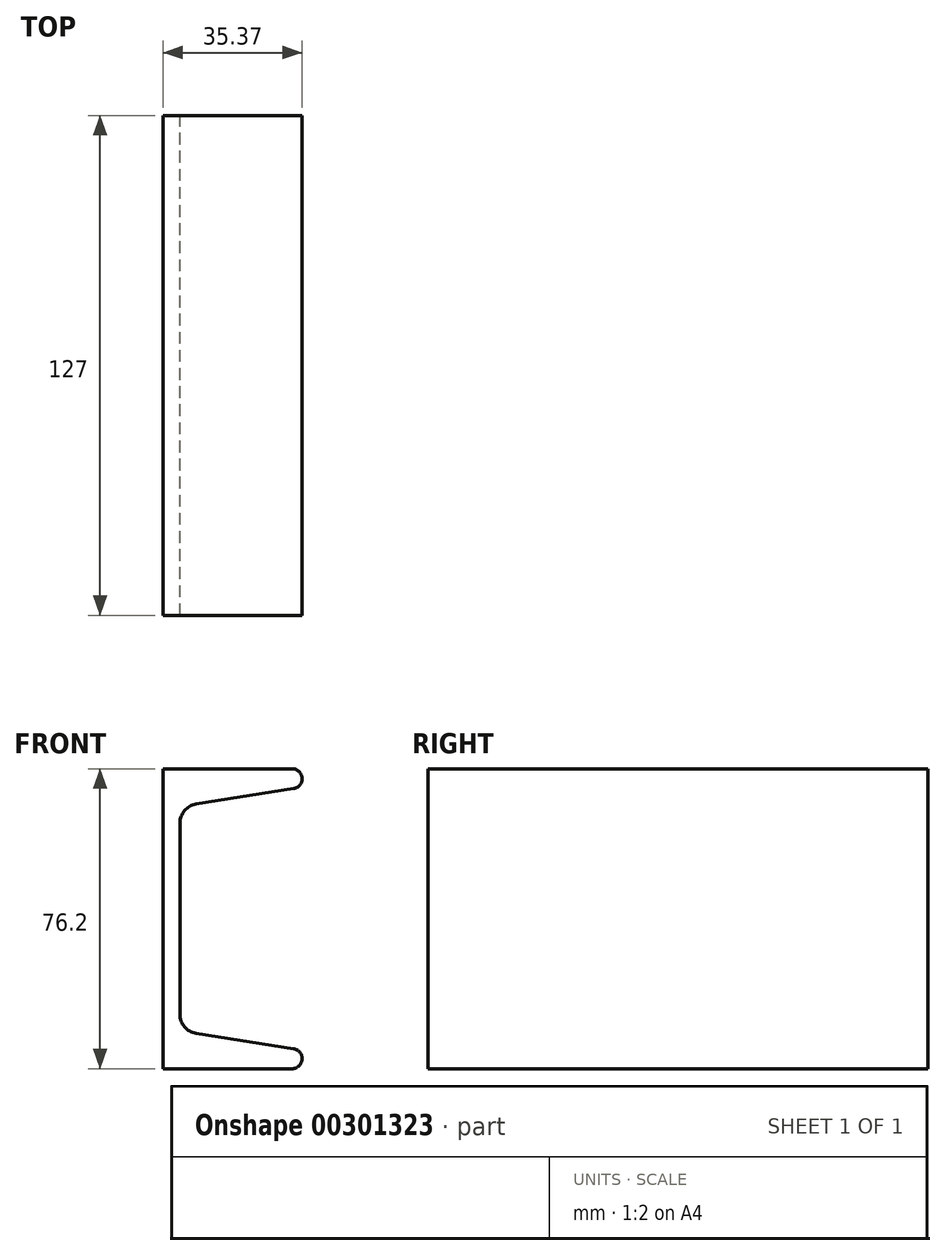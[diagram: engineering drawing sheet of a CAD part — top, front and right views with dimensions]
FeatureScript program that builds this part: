
annotation { "Feature Type Name" : "Feature", "Feature Type Description" : "" }
export const myFeature = defineFeature(function(context is Context, id is Id, definition is map)
    precondition{}
    {
        {
            var Q0;
            Q0=qCreatedBy(makeId("Front.planeOp"),FACE);
            var sketch = newSketch(context, id + "F0", { "sketchPlane" : qUnion([Q0])});
            skLineSegment(sketch, "E0", {"start": v(0, 0) * mm, "end": v(0, 76.2) * mm});
            skLineSegment(sketch, "E1", {"start": v(0, 76.2) * mm, "end": v(32.83, 76.2) * mm});
            skLineSegment(sketch, "E2", {"start": v(0, 0) * mm, "end": v(32.83, 0) * mm});
            skLineSegment(sketch, "E3", {"start": v(33.22, 71.15) * mm, "end": v(8.41, 67.22) * mm});
            skLineSegment(sketch, "E4", {"start": v(4.32, 62.43) * mm, "end": v(4.32, 13.77) * mm});
            skLineSegment(sketch, "E5", {"start": v(8.41, 8.98) * mm, "end": v(33.22, 5.05) * mm});
            skPoint(sketch, "E6.visualSharp", {"position": v(65.1, 76.2) * mm});
            skArc(sketch, "E6.filletArc", {"start": v(33.22, 71.15) * mm, "mid": v(35.36, 73.86) * mm, "end": v(32.83, 76.2) * mm});
            skPoint(sketch, "E7.visualSharp", {"position": v(65.1, 0) * mm});
            skArc(sketch, "E7.filletArc", {"start": v(32.83, 0) * mm, "mid": v(35.36, 2.34) * mm, "end": v(33.22, 5.05) * mm});
            skPoint(sketch, "E8.visualSharp", {"position": v(4.32, 66.57) * mm});
            skArc(sketch, "E8.filletArc", {"start": v(8.41, 67.22) * mm, "mid": v(5.48, 65.58) * mm, "end": v(4.32, 62.43) * mm});
            skPoint(sketch, "E9.visualSharp", {"position": v(4.32, 9.63) * mm});
            skArc(sketch, "E9.filletArc", {"start": v(4.32, 13.77) * mm, "mid": v(5.48, 10.62) * mm, "end": v(8.41, 8.98) * mm});
            skSolve(sketch);
        }
        {
            var Q0;
            Q0=makeQuery(id+"F0.imprint","IMPRINT",FACE,{"disambiguationData":[TD([[makeQuery(id+"F0.imprint","IMPRINT",EDGE,{"derivedFrom":sQuery(id+"F0.wireOp",EDGE,"E0")}),-1.0]])]});
            extrude(context, id + "F1", {"entities" : qUnion([Q0]), "depth" : 127 * mm});
        }
    });
